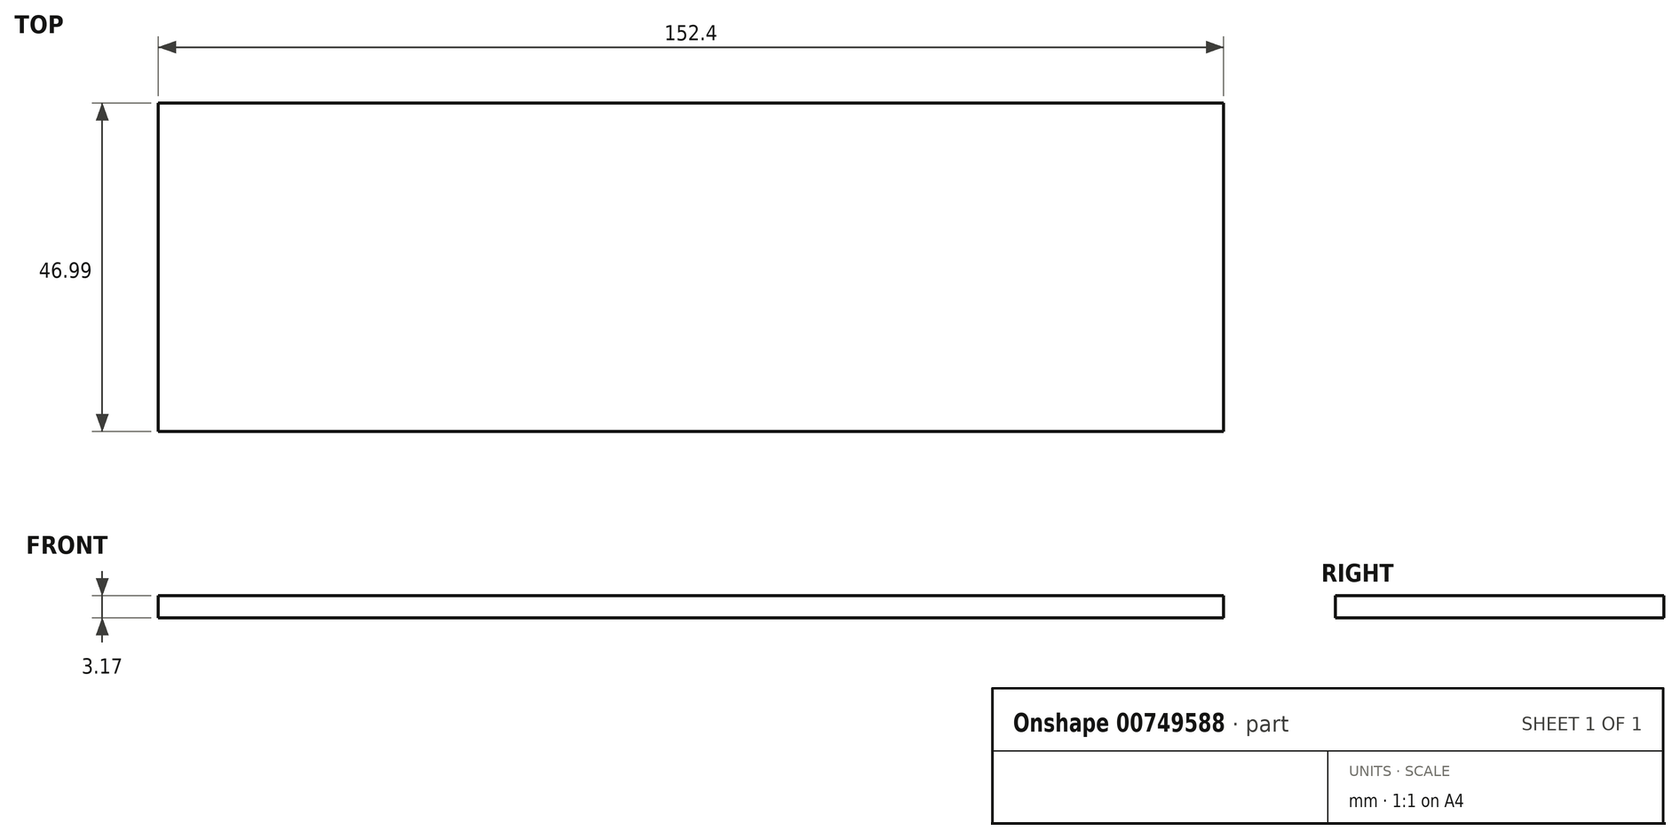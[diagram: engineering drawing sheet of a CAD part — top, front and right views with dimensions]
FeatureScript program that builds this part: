
annotation { "Feature Type Name" : "Feature", "Feature Type Description" : "" }
export const myFeature = defineFeature(function(context is Context, id is Id, definition is map)
    precondition{}
    {
        {
            var Q0;
            Q0=qCreatedBy(makeId("Top.planeOp"),FACE);
            var sketch = newSketch(context, id + "F0", { "sketchPlane" : qUnion([Q0])});
            skLineSegment(sketch, "E0.bottom", {"start": v(0, 0) * mm, "end": v(152.4, 0) * mm});
            skLineSegment(sketch, "E0.top", {"start": v(0, 47) * mm, "end": v(152.4, 47) * mm});
            skLineSegment(sketch, "E0.left", {"start": v(0, 0) * mm, "end": v(0, 47) * mm});
            skLineSegment(sketch, "E0.right", {"start": v(152.4, 0) * mm, "end": v(152.4, 47) * mm});
            skSolve(sketch);
        }
        {
            var Q0;
            Q0 = qSketchRegion(id + "F0", true);
            extrude(context, id + "F1", {"entities" : qUnion([Q0]), "depth" : 3.17 * mm, "offsetDistance" : 25.4 * mm});
        }
    });
